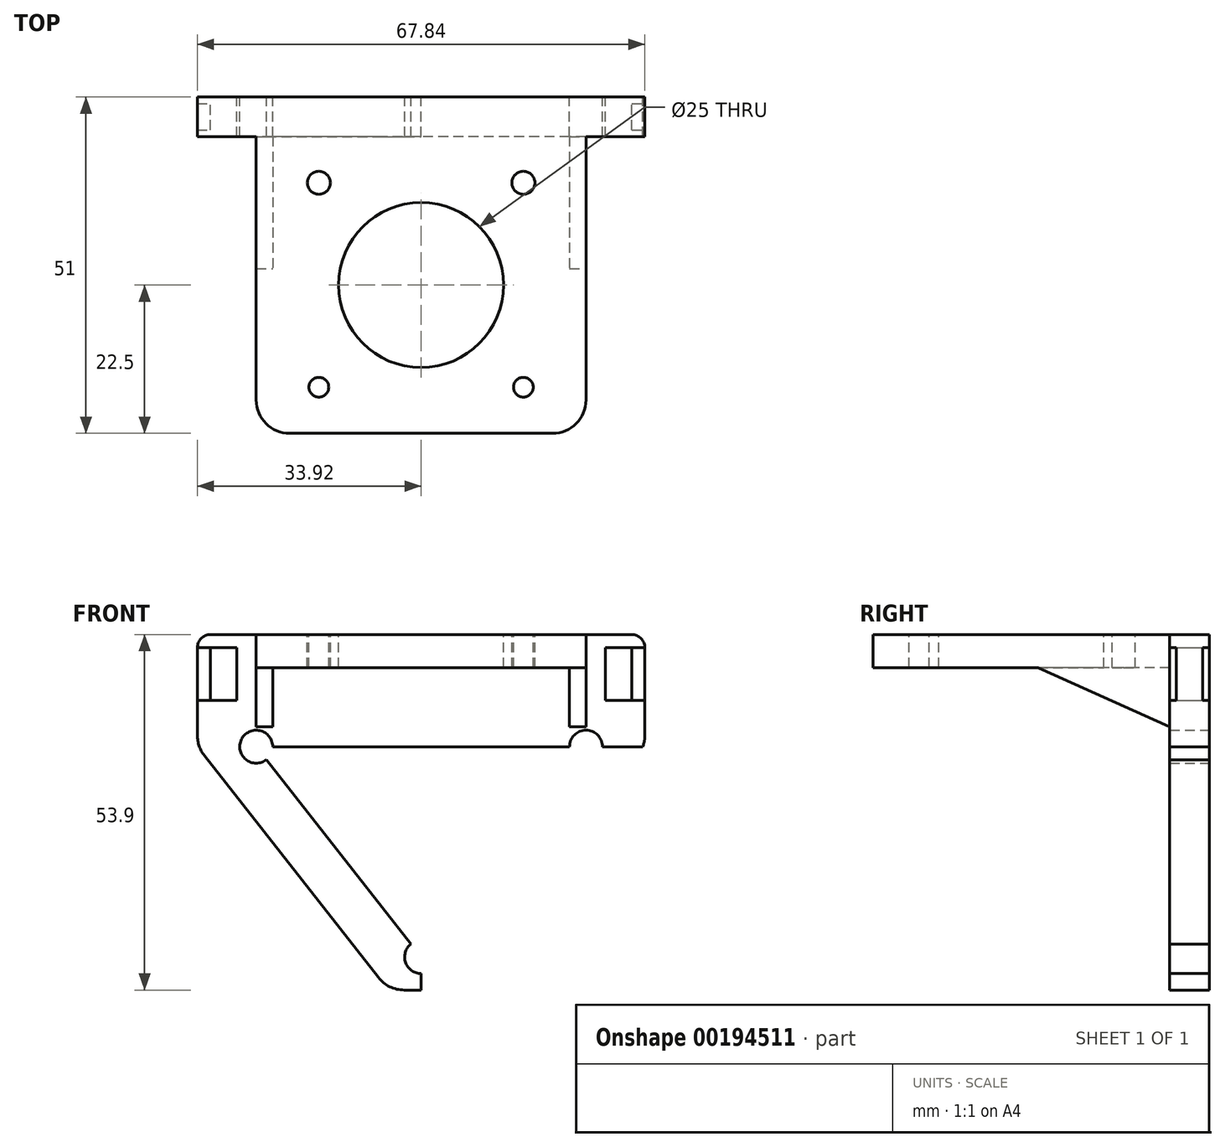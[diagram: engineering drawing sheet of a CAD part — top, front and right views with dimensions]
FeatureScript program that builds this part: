
annotation { "Feature Type Name" : "Feature", "Feature Type Description" : "" }
export const myFeature = defineFeature(function(context is Context, id is Id, definition is map)
    precondition{}
    {
        {
            var Q0;
            Q0=qCreatedBy(makeId("Front.planeOp"),FACE);
            var sketch = newSketch(context, id + "F0", { "sketchPlane" : qUnion([Q0])});
            skPoint(sketch, "E0.middle", {"position": v(0, 0) * mm});
            skPoint(sketch, "E1", {"position": v(0, -16.72) * mm});
            skLineSegment(sketch, "E2", {"start": v(-15.95, 15.18) * mm, "end": v(15.95, 15.18) * mm});
            skLineSegment(sketch, "E3", {"start": v(25, 15.18) * mm, "end": v(15.95, 15.18) * mm});
            skLineSegment(sketch, "E4", {"start": v(-15.95, 15.18) * mm, "end": v(-40.87, 15.18) * mm});
            skLineSegment(sketch, "E5", {"start": v(-76.54, 15.18) * mm, "end": v(86.17, 15.18) * mm});
            skPoint(sketch, "E6", {"position": v(0, 15.18) * mm});
            skPoint(sketch, "E7", {"position": v(25, 15.18) * mm});
            skPoint(sketch, "E8.MirrorP", {"position": v(-25, 15.18) * mm});
            skCircle(sketch, "E9", {"center": v(0, -16.72) * mm, "radius": 2.5 * mm});
            skCircle(sketch, "E10", {"center": v(25, 15.18) * mm, "radius": 2.5 * mm});
            skCircle(sketch, "E11", {"center": v(-25, 15.18) * mm, "radius": 2.5 * mm});
            skLineSegment(sketch, "E12", {"start": v(0, -16.72) * mm, "end": v(0, -21.72) * mm});
            skLineSegment(sketch, "E13", {"start": v(0, -21.72) * mm, "end": v(5, -21.72) * mm});
            skLineSegment(sketch, "E14", {"start": v(2.57, -21.72) * mm, "end": v(0, -21.72) * mm});
            skLineSegment(sketch, "E15", {"start": v(0, -21.72) * mm, "end": v(-2.57, -21.72) * mm});
            skLineSegment(sketch, "E16", {"start": v(-25, 15.18) * mm, "end": v(0, -16.72) * mm});
            skLineSegment(sketch, "E17", {"start": v(0, -16.72) * mm, "end": v(25, 15.18) * mm});
            skLineSegment(sketch, "E18", {"start": v(-25, 15.18) * mm, "end": v(25, 15.18) * mm});
            skLineSegment(sketch, "E19", {"start": v(6.5, -19.8) * mm, "end": v(32.85, 13.82) * mm});
            skLineSegment(sketch, "E20", {"start": v(-6.5, -19.8) * mm, "end": v(-32.85, 13.82) * mm});
            skLineSegment(sketch, "E21", {"start": v(-33.92, 16.9) * mm, "end": v(-33.92, 18.9) * mm});
            skLineSegment(sketch, "E22", {"start": v(33.92, 19.3) * mm, "end": v(33.92, 16.9) * mm});
            skPoint(sketch, "E23.visualSharp", {"position": v(33.92, 15.18) * mm});
            skArc(sketch, "E23.filletArc", {"start": v(32.85, 13.82) * mm, "mid": v(33.64, 15.27) * mm, "end": v(33.92, 16.9) * mm});
            skPoint(sketch, "E24.visualSharp", {"position": v(5, -21.72) * mm});
            skArc(sketch, "E24.filletArc", {"start": v(2.57, -21.72) * mm, "mid": v(4.75, -21.22) * mm, "end": v(6.5, -19.8) * mm});
            skPoint(sketch, "E25.visualSharp", {"position": v(-5, -21.72) * mm});
            skArc(sketch, "E25.filletArc", {"start": v(-6.5, -19.8) * mm, "mid": v(-4.75, -21.22) * mm, "end": v(-2.57, -21.72) * mm});
            skPoint(sketch, "E26.visualSharp", {"position": v(-33.92, 15.18) * mm});
            skArc(sketch, "E26.filletArc", {"start": v(-33.92, 16.9) * mm, "mid": v(-33.64, 15.27) * mm, "end": v(-32.85, 13.82) * mm});
            skLineSegment(sketch, "E27", {"start": v(-32.64, 20.18) * mm, "end": v(33.04, 20.18) * mm});
            skPoint(sketch, "E28.visualSharp", {"position": v(33.92, 20.18) * mm});
            skPoint(sketch, "E29.visualSharp", {"position": v(-33.92, 20.18) * mm});
            skLineSegment(sketch, "E30", {"start": v(33.92, 19.3) * mm, "end": v(33.92, 20.18) * mm});
            skLineSegment(sketch, "E31", {"start": v(33.92, 20.18) * mm, "end": v(33.04, 20.18) * mm});
            skLineSegment(sketch, "E32", {"start": v(-32.64, 20.18) * mm, "end": v(-33.92, 20.18) * mm});
            skLineSegment(sketch, "E33", {"start": v(-33.92, 20.18) * mm, "end": v(-33.92, 18.9) * mm});
            skLineSegment(sketch, "E34", {"start": v(33.92, 20.18) * mm, "end": v(33.92, 30.18) * mm});
            skLineSegment(sketch, "E35", {"start": v(-33.92, 20.18) * mm, "end": v(-33.92, 30.18) * mm});
            skLineSegment(sketch, "E36", {"start": v(-31.92, 32.18) * mm, "end": v(31.92, 32.18) * mm});
            skPoint(sketch, "E37", {"position": v(33.92, 30.18) * mm});
            skPoint(sketch, "E38", {"position": v(33.92, 22.18) * mm});
            skLineSegment(sketch, "E39", {"start": v(33.92, 30.18) * mm, "end": v(31.92, 30.18) * mm});
            skLineSegment(sketch, "E40", {"start": v(33.92, 22.18) * mm, "end": v(31.92, 22.18) * mm});
            skLineSegment(sketch, "E41", {"start": v(31.92, 22.18) * mm, "end": v(27.92, 22.18) * mm});
            skLineSegment(sketch, "E42", {"start": v(31.92, 30.18) * mm, "end": v(27.92, 30.18) * mm});
            skLineSegment(sketch, "E43", {"start": v(31.92, 22.18) * mm, "end": v(31.92, 30.18) * mm});
            skLineSegment(sketch, "E44", {"start": v(27.92, 22.18) * mm, "end": v(27.92, 30.18) * mm});
            skLineSegment(sketch, "E45.MirrorCS", {"start": v(-31.92, 22.18) * mm, "end": v(-31.92, 30.18) * mm});
            skLineSegment(sketch, "E46.MirrorCS", {"start": v(-31.92, 30.18) * mm, "end": v(-27.92, 30.18) * mm});
            skLineSegment(sketch, "E47.MirrorCS", {"start": v(-27.92, 22.18) * mm, "end": v(-27.92, 30.18) * mm});
            skLineSegment(sketch, "E48.MirrorCS", {"start": v(-31.92, 22.18) * mm, "end": v(-27.92, 22.18) * mm});
            skPoint(sketch, "E49.visualSharp", {"position": v(-33.92, 32.18) * mm});
            skArc(sketch, "E49.filletArc", {"start": v(-31.92, 32.18) * mm, "mid": v(-33.33, 31.6) * mm, "end": v(-33.92, 30.18) * mm});
            skPoint(sketch, "E50.visualSharp", {"position": v(33.92, 32.18) * mm});
            skArc(sketch, "E50.filletArc", {"start": v(33.92, 30.18) * mm, "mid": v(33.33, 31.6) * mm, "end": v(31.92, 32.18) * mm});
            skSolve(sketch);
        }
        {
            var Q0;
            {var subQ7=sQuery(id+"F0.wireOp",EDGE,"8j6oBXik-OWv6-CMHD-DYEs-HWpgqFpZJmO8");Q0=makeQuery(id+"F0.imprint","IMPRINT",FACE,{"disambiguationData":[TD([[makeQuery(id+"F0.imprint","IMPRINT",EDGE,{"derivedFrom":subQ7}),-1.0]])]});}
            var Q1;
            {var subQ0=sQuery(id+"F0.wireOp",EDGE,"PW2OsFPN-24ZK-WMl3-7S3p-6c8LhZ0Et7YX");var subQ5=sQuery(id+"F0.wireOp",EDGE,"jJSWg2bN-Z1GW-aEuE-efO0-1qQVljQy0SO1");var subQ6=makeQuery(id+"F0.imprint","INTERSECT",VERTEX,{"derivedFrom":[subQ5,subQ0]});Q1=makeQuery(id+"F0.imprint","IMPRINT",FACE,{"disambiguationData":[TD([[makeQuery(id+"F0.imprint","IMPRINT",EDGE,{"disambiguationData":[TD([[subQ6,-1.0]])],"derivedFrom":subQ5}),1.0]])]});}
            var Q2;
            {var subQ1=sQuery(id+"F0.wireOp",EDGE,"A9Tc2tPI-QaK9-aB4s-dhMC-U80szrhvGWtR");Q2=makeQuery(id+"F0.imprint","IMPRINT",FACE,{"disambiguationData":[TD([[makeQuery(id+"F0.imprint","IMPRINT",EDGE,{"derivedFrom":subQ1}),1.0]])]});}
            var Q3;
            {var subQ8=sQuery(id+"F0.wireOp",EDGE,"E21");Q3=makeQuery(id+"F0.imprint","IMPRINT",FACE,{"disambiguationData":[TD([[makeQuery(id+"F0.imprint","IMPRINT",EDGE,{"derivedFrom":subQ8}),-1.0]])]});}
            var Q4;
            {var subQ5=sQuery(id+"F0.wireOp",EDGE,"E18");var subQ6=makeQuery(id+"F0.imprint","IMPRINT",VERTEX,{"disambiguationData":[OD(0.0)],"derivedFrom":subQ5});Q4=makeQuery(id+"F0.imprint","IMPRINT",FACE,{"disambiguationData":[TD([[makeQuery(id+"F0.imprint","IMPRINT",EDGE,{"disambiguationData":[TD([[subQ6,-1.0]])],"derivedFrom":subQ5}),-1.0]])]});}
            var Q5;
            {var subQ0=sQuery(id+"F0.wireOp",EDGE,"E14");Q5=makeQuery(id+"F0.imprint","IMPRINT",FACE,{"disambiguationData":[TD([[makeQuery(id+"F0.imprint","IMPRINT",EDGE,{"derivedFrom":subQ0}),-1.0]])]});}
            var Q6;
            {var subQ0=sQuery(id+"F0.wireOp",EDGE,"E15");Q6=makeQuery(id+"F0.imprint","IMPRINT",FACE,{"disambiguationData":[TD([[makeQuery(id+"F0.imprint","IMPRINT",EDGE,{"derivedFrom":subQ0}),-1.0]])]});}
            var Q7;
            Q7=makeQuery(id+"F0.imprint","IMPRINT",FACE,{"disambiguationData":[TD([[makeQuery(id+"F0.imprint","IMPRINT",EDGE,{"derivedFrom":sQuery(id+"F0.wireOp",EDGE,"E27")}),1.0]])]});
            var Q8;
            {var subQ0=sQuery(id+"F0.wireOp",EDGE,"E39");Q8=makeQuery(id+"F0.imprint","IMPRINT",FACE,{"disambiguationData":[TD([[makeQuery(id+"F0.imprint","IMPRINT",EDGE,{"derivedFrom":subQ0}),1.0]])]});}
            extrude(context, id + "F1", {"entities" : qUnion([Q0, Q1, Q2, Q3, Q4, Q5, Q6, Q7, Q8]), "depth" : 6 * mm});
        }
        {
            var Q0;
            Q0=makeQuery(id+"F1.opExtrude","CAP_FACE",FACE,{"disambiguationData":[OSD([sQuery(id+"F0.wireOp",EDGE,"E9"),sQuery(id+"F0.wireOp",EDGE,"E10"),sQuery(id+"F0.wireOp",EDGE,"E11"),sQuery(id+"F0.wireOp",EDGE,"E14"),sQuery(id+"F0.wireOp",EDGE,"E15"),sQuery(id+"F0.wireOp",EDGE,"E19"),sQuery(id+"F0.wireOp",EDGE,"E20"),sQuery(id+"F0.wireOp",EDGE,"E21"),sQuery(id+"F0.wireOp",EDGE,"E22"),sQuery(id+"F0.wireOp",EDGE,"E23.filletArc"),sQuery(id+"F0.wireOp",EDGE,"E24.filletArc"),sQuery(id+"F0.wireOp",EDGE,"E25.filletArc"),sQuery(id+"F0.wireOp",EDGE,"E26.filletArc"),sQuery(id+"F0.wireOp",EDGE,"E30"),sQuery(id+"F0.wireOp",EDGE,"E33"),sQuery(id+"F0.wireOp",EDGE,"E34"),sQuery(id+"F0.wireOp",EDGE,"E35"),sQuery(id+"F0.wireOp",EDGE,"E36"),sQuery(id+"F0.wireOp",EDGE,"E41"),sQuery(id+"F0.wireOp",EDGE,"E42"),sQuery(id+"F0.wireOp",EDGE,"E43"),sQuery(id+"F0.wireOp",EDGE,"E44"),sQuery(id+"F0.wireOp",EDGE,"E45.MirrorCS"),sQuery(id+"F0.wireOp",EDGE,"E46.MirrorCS"),sQuery(id+"F0.wireOp",EDGE,"E47.MirrorCS"),sQuery(id+"F0.wireOp",EDGE,"E48.MirrorCS")])],"isStart":true});
            var sketch = newSketch(context, id + "F2", { "sketchPlane" : qUnion([Q0])});
            skLineSegment(sketch, "E51", {"start": v(-31.92, 22.18) * mm, "end": v(-33.92, 22.18) * mm});
            skLineSegment(sketch, "E52", {"start": v(-31.92, 30.18) * mm, "end": v(-33.92, 30.18) * mm});
            skLineSegment(sketch, "E53", {"start": v(-33.92, 30.18) * mm, "end": v(-33.92, 22.18) * mm});
            skLineSegment(sketch, "E54", {"start": v(31.92, 30.18) * mm, "end": v(33.92, 30.18) * mm});
            skLineSegment(sketch, "E55", {"start": v(33.92, 30.18) * mm, "end": v(33.92, 22.18) * mm});
            skLineSegment(sketch, "E56", {"start": v(33.92, 22.18) * mm, "end": v(31.92, 22.18) * mm});
            skLineSegment(sketch, "E57", {"start": v(31.92, 22.18) * mm, "end": v(31.92, 30.18) * mm});
            skLineSegment(sketch, "E58", {"start": v(-31.92, 22.18) * mm, "end": v(-31.92, 30.18) * mm});
            skSolve(sketch);
        }
        {
            var Q0;
            Q0 = qSketchRegion(id + "F2", true);
            var Q1;
            Q1=makeQuery(id+"F2.imprint","IMPRINT",FACE,{"disambiguationData":[TD([[makeQuery(id+"F2.imprint","IMPRINT",EDGE,{"derivedFrom":sQuery(id+"F2.wireOp",EDGE,"E51")}),-1.0]])]});
            extrude(context, id + "F3", {"entities" : qUnion([Q0, Q1]), "operationType" : NewBodyOperationType.REMOVE, "oppositeDirection" : true, "depth" : 1 * mm});
        }
        {
            var Q0;
            Q0=makeQuery(id+"F1.opExtrude","CAP_FACE",FACE,{"disambiguationData":[OSD([sQuery(id+"F0.wireOp",EDGE,"E9"),sQuery(id+"F0.wireOp",EDGE,"E10"),sQuery(id+"F0.wireOp",EDGE,"E11"),sQuery(id+"F0.wireOp",EDGE,"E14"),sQuery(id+"F0.wireOp",EDGE,"E15"),sQuery(id+"F0.wireOp",EDGE,"E19"),sQuery(id+"F0.wireOp",EDGE,"E20"),sQuery(id+"F0.wireOp",EDGE,"E21"),sQuery(id+"F0.wireOp",EDGE,"E22"),sQuery(id+"F0.wireOp",EDGE,"E23.filletArc"),sQuery(id+"F0.wireOp",EDGE,"E24.filletArc"),sQuery(id+"F0.wireOp",EDGE,"E25.filletArc"),sQuery(id+"F0.wireOp",EDGE,"E26.filletArc"),sQuery(id+"F0.wireOp",EDGE,"E30"),sQuery(id+"F0.wireOp",EDGE,"E33"),sQuery(id+"F0.wireOp",EDGE,"E34"),sQuery(id+"F0.wireOp",EDGE,"E35"),sQuery(id+"F0.wireOp",EDGE,"E36"),sQuery(id+"F0.wireOp",EDGE,"E41"),sQuery(id+"F0.wireOp",EDGE,"E42"),sQuery(id+"F0.wireOp",EDGE,"E43"),sQuery(id+"F0.wireOp",EDGE,"E44"),sQuery(id+"F0.wireOp",EDGE,"E45.MirrorCS"),sQuery(id+"F0.wireOp",EDGE,"E46.MirrorCS"),sQuery(id+"F0.wireOp",EDGE,"E47.MirrorCS"),sQuery(id+"F0.wireOp",EDGE,"E48.MirrorCS")])],"isStart":false});
            var sketch = newSketch(context, id + "F4", { "sketchPlane" : qUnion([Q0])});
            skLineSegment(sketch, "E59", {"start": v(-31.92, 30.18) * mm, "end": v(-33.92, 30.18) * mm});
            skLineSegment(sketch, "E60", {"start": v(-33.92, 30.18) * mm, "end": v(-33.92, 22.18) * mm});
            skLineSegment(sketch, "E61", {"start": v(-33.92, 22.18) * mm, "end": v(-31.92, 22.18) * mm});
            skLineSegment(sketch, "E62", {"start": v(-31.92, 22.18) * mm, "end": v(-31.92, 30.18) * mm});
            skLineSegment(sketch, "E63", {"start": v(31.92, 22.18) * mm, "end": v(33.92, 22.18) * mm});
            skLineSegment(sketch, "E64", {"start": v(33.92, 22.18) * mm, "end": v(33.92, 30.18) * mm});
            skLineSegment(sketch, "E65", {"start": v(33.92, 30.18) * mm, "end": v(31.92, 30.18) * mm});
            skLineSegment(sketch, "E66", {"start": v(31.92, 30.18) * mm, "end": v(31.92, 22.18) * mm});
            skSolve(sketch);
        }
        {
            var Q0;
            Q0 = qSketchRegion(id + "F4", true);
            extrude(context, id + "F5", {"entities" : qUnion([Q0]), "operationType" : NewBodyOperationType.REMOVE, "oppositeDirection" : true, "depth" : 1 * mm});
        }
        {
            var Q0;
            Q0=makeQuery(id+"F1.opExtrude","CAP_FACE",FACE,{"disambiguationData":[OSD([sQuery(id+"F0.wireOp",EDGE,"E9"),sQuery(id+"F0.wireOp",EDGE,"E10"),sQuery(id+"F0.wireOp",EDGE,"E11"),sQuery(id+"F0.wireOp",EDGE,"E14"),sQuery(id+"F0.wireOp",EDGE,"E15"),sQuery(id+"F0.wireOp",EDGE,"E19"),sQuery(id+"F0.wireOp",EDGE,"E20"),sQuery(id+"F0.wireOp",EDGE,"E21"),sQuery(id+"F0.wireOp",EDGE,"E22"),sQuery(id+"F0.wireOp",EDGE,"E23.filletArc"),sQuery(id+"F0.wireOp",EDGE,"E24.filletArc"),sQuery(id+"F0.wireOp",EDGE,"E25.filletArc"),sQuery(id+"F0.wireOp",EDGE,"E26.filletArc"),sQuery(id+"F0.wireOp",EDGE,"E30"),sQuery(id+"F0.wireOp",EDGE,"E33"),sQuery(id+"F0.wireOp",EDGE,"E34"),sQuery(id+"F0.wireOp",EDGE,"E35"),sQuery(id+"F0.wireOp",EDGE,"E36"),sQuery(id+"F0.wireOp",EDGE,"E41"),sQuery(id+"F0.wireOp",EDGE,"E42"),sQuery(id+"F0.wireOp",EDGE,"E43"),sQuery(id+"F0.wireOp",EDGE,"E44"),sQuery(id+"F0.wireOp",EDGE,"E45.MirrorCS"),sQuery(id+"F0.wireOp",EDGE,"E46.MirrorCS"),sQuery(id+"F0.wireOp",EDGE,"E47.MirrorCS"),sQuery(id+"F0.wireOp",EDGE,"E48.MirrorCS"),sQuery(id+"F0.wireOp",EDGE,"E49.filletArc"),sQuery(id+"F0.wireOp",EDGE,"E50.filletArc")])],"isStart":false});
            var sketch = newSketch(context, id + "F6", { "sketchPlane" : qUnion([Q0])});
            skLineSegment(sketch, "E67", {"start": v(0, 0) * mm, "end": v(0, 32.18) * mm});
            skLineSegment(sketch, "E68", {"start": v(0, 32.18) * mm, "end": v(25, 32.18) * mm});
            skLineSegment(sketch, "E69", {"start": v(0, 32.18) * mm, "end": v(-25, 32.18) * mm});
            skLineSegment(sketch, "E70", {"start": v(-25, 32.18) * mm, "end": v(-25, 27.18) * mm});
            skLineSegment(sketch, "E71", {"start": v(-25, 27.18) * mm, "end": v(25, 27.18) * mm});
            skLineSegment(sketch, "E72", {"start": v(25, 27.18) * mm, "end": v(25, 32.18) * mm});
            skSolve(sketch);
        }
        {
            var Q0;
            Q0 = qSketchRegion(id + "F6", true);
            extrude(context, id + "F7", {"entities" : qUnion([Q0]), "operationType" : NewBodyOperationType.ADD, "depth" : 45 * mm, "offsetDistance" : 25.4 * mm});
        }
        {
            var Q0;
            Q0=makeQuery(id+"F7.opExtrude","CAP_EDGE",EDGE,{"disambiguationData":[OSD([sQuery(id+"F6.wireOp",EDGE,"E72")])],"isStart":false});
            var Q1;
            Q1=makeQuery(id+"F7.opExtrude","CAP_EDGE",EDGE,{"disambiguationData":[OSD([sQuery(id+"F6.wireOp",EDGE,"E70")])],"isStart":false});
            fillet(context, id + "F8", {"entities" : qUnion([Q0, Q1]), "radius" : 5.08 * mm, "tangentPropagation" : true, "allowEdgeOverflow" : false});
        }
        {
            var Q0;
            Q0=makeQuery(id+"F7.opExtrude","SWEPT_FACE",FACE,{"disambiguationData":[OSD([sQuery(id+"F6.wireOp",EDGE,"E71")])]});
            var sketch = newSketch(context, id + "F9", { "sketchPlane" : qUnion([Q0])});
            skLineSegment(sketch, "E73", {"start": v(0, 6) * mm, "end": v(22.5, 6) * mm});
            skLineSegment(sketch, "E74.MirrorCS", {"start": v(0, 6) * mm, "end": v(-22.5, 6) * mm});
            skLineSegment(sketch, "E75", {"start": v(-22.5, 6) * mm, "end": v(-22.5, 26) * mm});
            skLineSegment(sketch, "E76", {"start": v(22.5, 6) * mm, "end": v(22.5, 26) * mm});
            skLineSegment(sketch, "E77", {"start": v(22.5, 26) * mm, "end": v(25, 26) * mm});
            skLineSegment(sketch, "E78", {"start": v(25, 26) * mm, "end": v(25, 6) * mm});
            skLineSegment(sketch, "E79", {"start": v(25, 6) * mm, "end": v(22.5, 6) * mm});
            skLineSegment(sketch, "E80", {"start": v(-22.5, 6) * mm, "end": v(-25, 6) * mm});
            skLineSegment(sketch, "E81", {"start": v(-25, 6) * mm, "end": v(-25, 26) * mm});
            skLineSegment(sketch, "E82", {"start": v(-25, 26) * mm, "end": v(-22.5, 26) * mm});
            skSolve(sketch);
        }
        {
            var Q0;
            Q0=makeQuery(id+"F9.imprint","IMPRINT",FACE,{"disambiguationData":[TD([[makeQuery(id+"F9.imprint","IMPRINT",EDGE,{"derivedFrom":sQuery(id+"F9.wireOp",EDGE,"E76")}),-1.0]])]});
            var Q1;
            Q1=makeQuery(id+"F9.imprint","IMPRINT",FACE,{"disambiguationData":[TD([[makeQuery(id+"F9.imprint","IMPRINT",EDGE,{"derivedFrom":sQuery(id+"F9.wireOp",EDGE,"E75")}),1.0]])]});
            extrude(context, id + "F10", {"entities" : qUnion([Q0, Q1]), "operationType" : NewBodyOperationType.ADD, "depth" : 9 * mm, "offsetDistance" : 25.4 * mm});
        }
        {
            var Q0;
            Q0=makeQuery(id+"F10.boolean.opBoolean","MERGE",FACE,{"derivedFrom":[makeQuery(id+"F7.opExtrude","SWEPT_FACE",FACE,{"disambiguationData":[OSD([sQuery(id+"F6.wireOp",EDGE,"E70")])]}),makeQuery(id+"F10.opExtrude","SWEPT_FACE",FACE,{"disambiguationData":[OSD([sQuery(id+"F9.wireOp",EDGE,"E81")])]})]});
            var sketch = newSketch(context, id + "F11", { "sketchPlane" : qUnion([Q0])});
            skLineSegment(sketch, "E83", {"start": v(6, 18.18) * mm, "end": v(26, 27.18) * mm});
            skLineSegment(sketch, "E84", {"start": v(26, 27.18) * mm, "end": v(26, 18.18) * mm});
            skLineSegment(sketch, "E85", {"start": v(26, 18.18) * mm, "end": v(6, 18.18) * mm});
            skSolve(sketch);
        }
        {
            var Q0;
            Q0 = qSketchRegion(id + "F11", true);
            extrude(context, id + "F12", {"entities" : qUnion([Q0]), "operationType" : NewBodyOperationType.REMOVE, "oppositeDirection" : true, "depth" : 50.3 * mm, "offsetDistance" : 25.4 * mm});
        }
        {
            var Q0;
            Q0=makeQuery(id+"F7.boolean.opBoolean","MERGE",FACE,{"derivedFrom":[makeQuery(id+"F1.opExtrude","SWEPT_FACE",FACE,{"disambiguationData":[OSD([sQuery(id+"F0.wireOp",EDGE,"E36")])]}),makeQuery(id+"F7.opExtrude","SWEPT_FACE",FACE,{"disambiguationData":[OSD([sQuery(id+"F6.wireOp",EDGE,"E68"),sQuery(id+"F6.wireOp",EDGE,"E69")])]})]});
            var sketch = newSketch(context, id + "F13", { "sketchPlane" : qUnion([Q0])});
            skCircle(sketch, "E86", {"center": v(0, -28.5) * mm, "radius": 12.5 * mm});
            skCircle(sketch, "E87", {"center": v(-15.5, -13) * mm, "radius": 1.75 * mm});
            skCircle(sketch, "E88", {"center": v(15.5, -13) * mm, "radius": 1.75 * mm});
            skCircle(sketch, "E89", {"center": v(15.5, -44) * mm, "radius": 1.5 * mm});
            skCircle(sketch, "E90", {"center": v(-15.5, -44) * mm, "radius": 1.5 * mm});
            skSolve(sketch);
        }
        {
            var Q0;
            Q0 = qSketchRegion(id + "F13", true);
            extrude(context, id + "F14", {"entities" : qUnion([Q0]), "operationType" : NewBodyOperationType.REMOVE, "oppositeDirection" : true, "depth" : 25.4 * mm, "offsetDistance" : 25.4 * mm});
        }
    });
